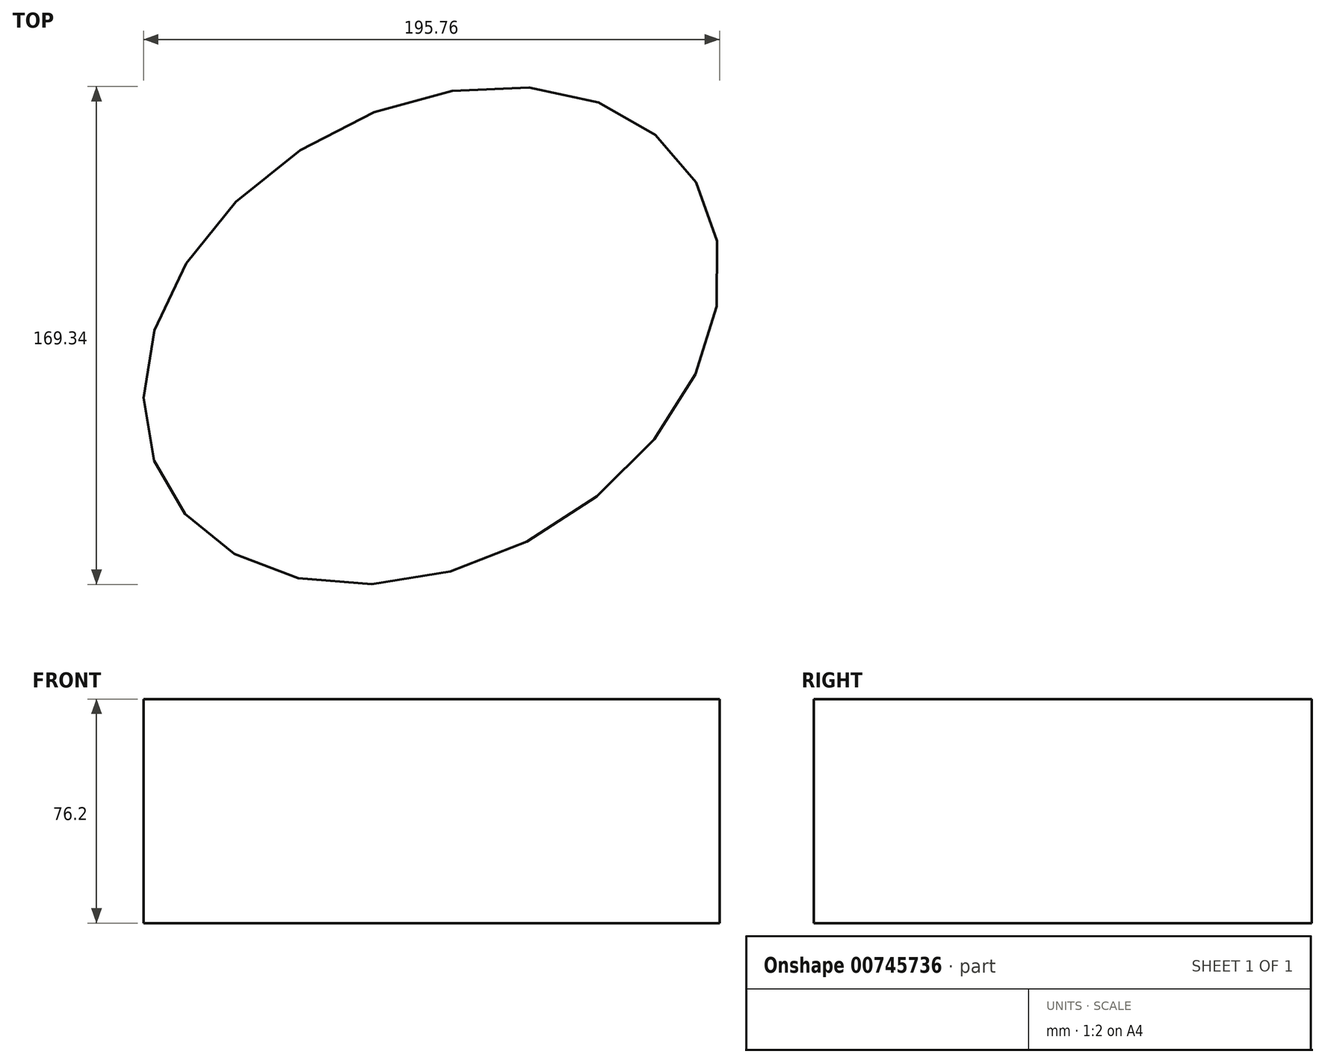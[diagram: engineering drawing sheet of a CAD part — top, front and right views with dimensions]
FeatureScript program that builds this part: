
annotation { "Feature Type Name" : "Feature", "Feature Type Description" : "" }
export const myFeature = defineFeature(function(context is Context, id is Id, definition is map)
    precondition{}
    {
        {
            var Q0;
            Q0=qCreatedBy(makeId("Top.planeOp"),FACE);
            var sketch = newSketch(context, id + "F0", { "sketchPlane" : qUnion([Q0])});
            skEllipse(sketch, "E0", {"center": v(0, 0) * mm, "majorRadius": 103.92 * mm, "minorRadius": 77.13 * mm, "majorAxis": v(0.87, 0.5)});
            skSolve(sketch);
        }
        {
            var Q0;
            Q0=makeQuery(id+"F0.imprint","IMPRINT",FACE,{"disambiguationData":[TD([[makeQuery(id+"F0.imprint","IMPRINT",EDGE,{"derivedFrom":sQuery(id+"F0.wireOp",EDGE,"E0")}),1.0]])]});
            extrude(context, id + "F1", {"entities" : qUnion([Q0]), "depth" : 76.2 * mm, "offsetDistance" : 25.4 * mm});
        }
    });
